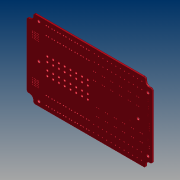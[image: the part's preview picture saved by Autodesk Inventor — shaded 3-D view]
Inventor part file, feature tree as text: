
AUTODESK INVENTOR PART (.ipt)
format: ipt  version: unknown  size: 1,277,952 bytes
history: native  units: mm (DEFAULTED — no unit token found)
features: imported_body x1, extrude x1, sketch x1, projected_geometry x1
ambient origin geometry x8: Origin, YZ Plane, XZ Plane, XY Plane, X Axis, Y Axis, Z Axis, Center Point
feature tree (4):
  imported_body  "Base1"
  extrude  "Extrusion1"  [1 undecoded]
  sketch  "Sketch1"  dims[d0=2.3876mm d1=0.0mm]
  projected_geometry  "Projected Loop1"
note: 1 required parameter value undecoded (feature->parameter linkage not recoverable at this tier; creation-order binding heuristic only, values carry confidence <= 0.55)
